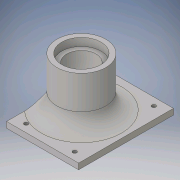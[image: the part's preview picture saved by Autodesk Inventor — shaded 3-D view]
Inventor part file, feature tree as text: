
AUTODESK INVENTOR PART (.ipt)
format: ipt  version: 2016 (Build 200138000, 138)  size: 180,736 bytes
history: native  units: in
note: dims shown in document units (in); Inventor stores cm internally (conversion verified against a paired STEP export)
features: sketch x6, extrude x5, hole x1, fillet x1
ambient origin geometry x8: Origin, YZ Plane, XZ Plane, XY Plane, X Axis, Y Axis, Z Axis, Center Point
bodies: Solid1 (feature_tree)
feature tree (13):
  extrude  "Extrusion1"  Depth=1.4488in
  hole  "Hole1"  [1 undecoded]
  extrude  "Extrusion2"  Depth=0.2362in
  extrude  "Extrusion3"  Depth=0.2362in
  extrude  "Extrusion4"  Depth=0.2362in
  extrude  "Extrusion5"  Depth=0.315in
  fillet  "Fillet2"  Radius=0.9528in
  sketch  "Sketch1"  dims[d0=1.9055in d1=1.4488in]
  sketch  "Sketch2"  dims[d2=0.1181in d3=0.0in d4=0.1575in]
  sketch  "Sketch3"  dims[d5=0.2362in d6=0.2362in]
  sketch  "Sketch4"  dims[d7=0.1575in d8=0.2362in]
  sketch  "Sketch5"  dims[d9=0.1575in d10=0.2362in]
  sketch  "Sketch8"  dims[d11=0.1575in d12=0.0787in d13=0.2362in d14=0.1575in d15=0.0787in d16=90.0deg d17=0.315in d18=0.8108in d19=0.5512in d20=0.9528in d21=0.9528in d22=0.5906in d23=0.9843in d24=0.9843in d25=0.0in d26=1.378in d27=0.0in d29=0.7874in d30=0.1575in d31=0.0in d32=0.7874in d33=0.1575in d34=0.0in d35=0.315in]
note: 1 required parameter value undecoded (feature->parameter linkage not recoverable at this tier; creation-order binding heuristic only, values carry confidence <= 0.55)
